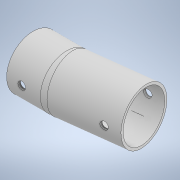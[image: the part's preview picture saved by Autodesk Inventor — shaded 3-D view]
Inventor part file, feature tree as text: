
AUTODESK INVENTOR PART (.ipt)
format: ipt  version: 2022 (Build 260153000, 153)  size: 246,272 bytes
history: native  units: mm
features: sketch x4, extrude x2, sweep x1
ambient origin geometry x8: Origin, YZ Plane, XZ Plane, XY Plane, X Axis, Y Axis, Z Axis, Center Point
bodies: Body1 (feature_tree)
feature tree (7):
  sweep  "Sweep1"
  extrude  "Extrusion8"  Depth=30.194196mm
  extrude  "Extrusion9"  Depth=10.0mm
  sketch  "Sketch5"  dims[d31=34.456mm d122=14.0mm]
  sketch  "Sketch6"  dims[d123=27.0mm d124=30.194196mm]
  sketch  "Sketch7"  dims[d125=10.0mm d126=19.0mm]
  sketch  "Sketch8"  dims[d127=21.0mm d128=0.0mm d129=0.0mm d130=6.0mm d131=3.0mm d132=25.0mm d133=0.0mm d134=6.0mm d135=3.0mm d136=25.0mm d137=0.0mm d138=0.01mm d139=0.01mm]
